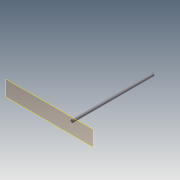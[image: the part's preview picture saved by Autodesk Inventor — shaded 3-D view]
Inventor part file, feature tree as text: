
AUTODESK INVENTOR PART (.ipt)
format: ipt  version: 2014 SP1 (Build 180222100, 222)  size: 66,048 bytes
history: native  units: in
note: dims shown in document units (in); Inventor stores cm internally (conversion verified against a paired STEP export)
features: plane x1, extrude x1, sketch x1, reference x1
ambient origin geometry x8: Origin, YZ Plane, XZ Plane, XY Plane, X Axis, Y Axis, Z Axis, Center Point
bodies: Solid1 (feature_tree)
feature tree (4):
  plane  "Work Plane1"
  extrude  "Extrusion1"  Depth=3.6024in TaperAngle=0.0deg
  sketch  "Sketch1"  dims[d0=0.1181in d1=3.6024in d2=0.0in]
  reference  "Reference1"
